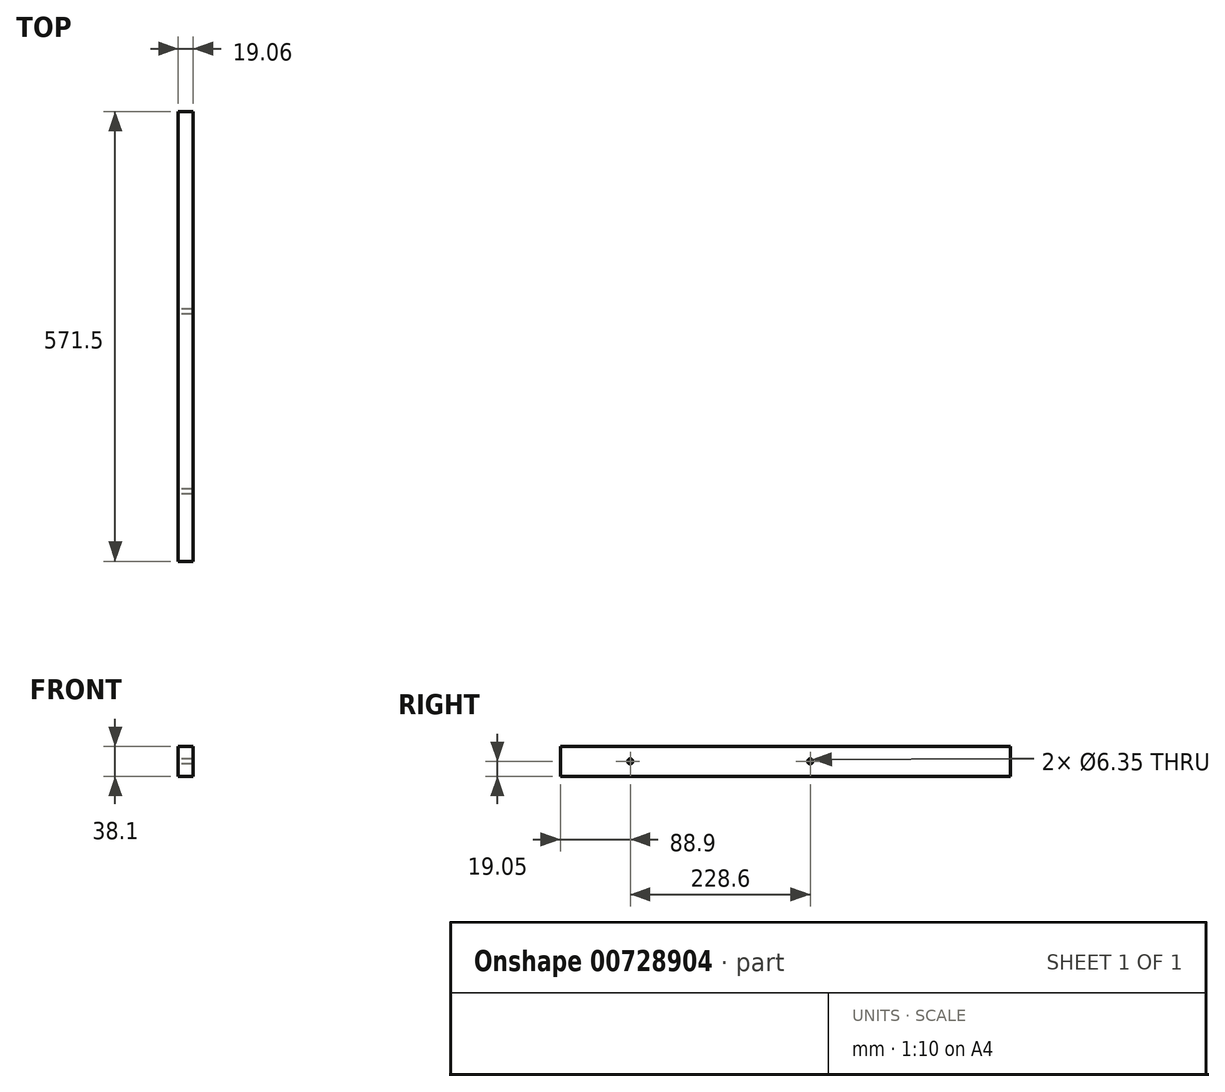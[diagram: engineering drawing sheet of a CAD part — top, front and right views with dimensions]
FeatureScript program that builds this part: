
annotation { "Feature Type Name" : "Feature", "Feature Type Description" : "" }
export const myFeature = defineFeature(function(context is Context, id is Id, definition is map)
    precondition{}
    {
        {
            var Q0;
            Q0=qCreatedBy(makeId("Front.planeOp"),FACE);
            var sketch = newSketch(context, id + "F0", { "sketchPlane" : qUnion([Q0])});
            skLineSegment(sketch, "E0.bottom", {"start": v(9.52, -19.05) * mm, "end": v(-9.53, -19.05) * mm});
            skLineSegment(sketch, "E0.top", {"start": v(9.52, 19.05) * mm, "end": v(-9.53, 19.05) * mm});
            skLineSegment(sketch, "E0.left", {"start": v(9.52, -19.05) * mm, "end": v(9.52, 19.05) * mm});
            skLineSegment(sketch, "E0.right", {"start": v(-9.53, -19.05) * mm, "end": v(-9.53, 19.05) * mm});
            skPoint(sketch, "E0.middle", {"position": v(0, 0) * mm});
            skSolve(sketch);
        }
        {
            var Q0;
            Q0=makeQuery(id+"F0.imprint","IMPRINT",FACE,{"disambiguationData":[TD([[makeQuery(id+"F0.imprint","IMPRINT",EDGE,{"derivedFrom":sQuery(id+"F0.wireOp",EDGE,"E0.bottom")}),-1.0]])]});
            extrude(context, id + "F1", {"entities" : qUnion([Q0]), "oppositeDirection" : true, "depth" : 571.5 * mm, "offsetDistance" : 25.4 * mm});
        }
        {
            var Q0;
            Q0=makeQuery(id+"F1.opExtrude","SWEPT_FACE",FACE,{"disambiguationData":[OSD([sQuery(id+"F0.wireOp",EDGE,"E0.left")])]});
            var sketch = newSketch(context, id + "F2", { "sketchPlane" : qUnion([Q0])});
            skPoint(sketch, "E1", {"position": v(88.9, 0) * mm});
            skPoint(sketch, "E2", {"position": v(317.5, 0) * mm});
            skSolve(sketch);
        }
        {
            var Q0;
            Q0=sQuery(id+"F2.wireOp",VERTEX,"E1");
            var Q1;
            Q1=sQuery(id+"F2.wireOp",VERTEX,"E2");
            var Q2;
            Q2=makeQuery(id+"F1.opExtrude","SWEPT_BODY",BODY,{"disambiguationData":[OSD([sQuery(id+"F0.wireOp",EDGE,"E0.bottom"),sQuery(id+"F0.wireOp",EDGE,"E0.top"),sQuery(id+"F0.wireOp",EDGE,"E0.left"),sQuery(id+"F0.wireOp",EDGE,"E0.right")])]});
            hole(context, id + "F3", {"style" : HoleStyle.SIMPLE, "endStyle" : HoleEndStyle.THROUGH, "holeDiameter" : 6.35 * mm, "majorDiameter" : 6.35 * mm, "isTappedThrough" : true, "tappedDepth" : 13.5 * mm, "tapClearance" : 3, "locations" : qUnion([Q0, Q1]), "scope" : qUnion([Q2]), "startStyle" : HoleStartStyle.PART});
        }
    });
